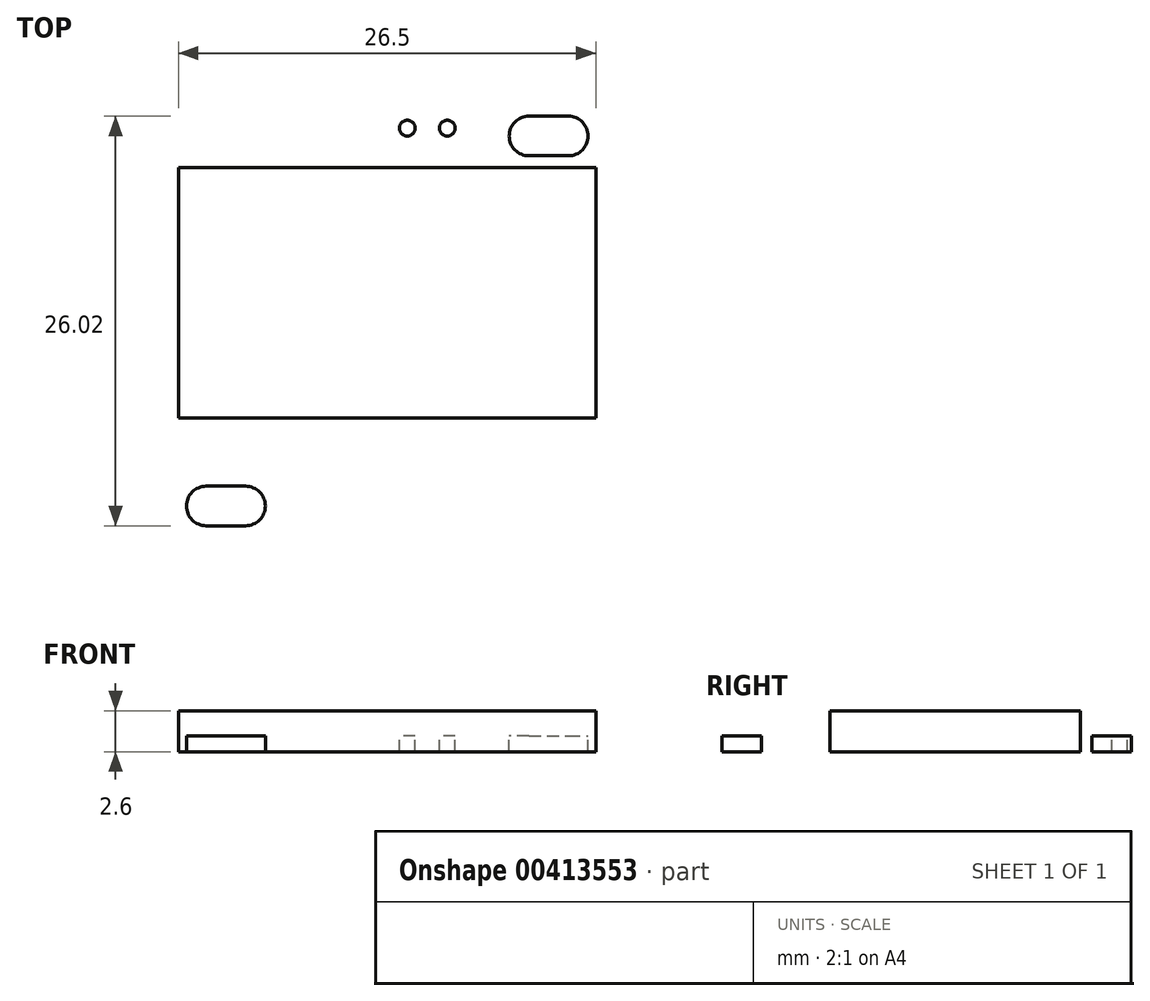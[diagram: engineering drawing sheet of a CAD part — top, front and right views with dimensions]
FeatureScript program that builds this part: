
annotation { "Feature Type Name" : "Feature", "Feature Type Description" : "" }
export const myFeature = defineFeature(function(context is Context, id is Id, definition is map)
    precondition{}
    {
        {
            var Q0;
            Q0=qCreatedBy(makeId("Top.planeOp"),FACE);
            var sketch = newSketch(context, id + "F0", { "sketchPlane" : qUnion([Q0])});
            skLineSegment(sketch, "E0.bottom", {"start": v(13.75, 13.75) * mm, "end": v(-13.75, 13.75) * mm});
            skLineSegment(sketch, "E0.top", {"start": v(13.75, -13.75) * mm, "end": v(-13.75, -13.75) * mm});
            skLineSegment(sketch, "E0.left", {"start": v(13.75, 13.75) * mm, "end": v(13.75, -13.75) * mm});
            skLineSegment(sketch, "E0.right", {"start": v(-13.75, 13.75) * mm, "end": v(-13.75, -13.75) * mm});
            skPoint(sketch, "E0.middle", {"position": v(0, 0) * mm});
            skSolve(sketch);
        }
        {
            var Q0;
            Q0 = qSketchRegion(id + "F0", true);
            extrude(context, id + "F1", {"entities" : qUnion([Q0]), "depth" : 1 * mm});
        }
        {
            var Q0;
            Q0=makeQuery(id+"F1.opExtrude","CAP_FACE",FACE,{"disambiguationData":[OSD([sQuery(id+"F0.wireOp",EDGE,"E0.bottom"),sQuery(id+"F0.wireOp",EDGE,"E0.top"),sQuery(id+"F0.wireOp",EDGE,"E0.left"),sQuery(id+"F0.wireOp",EDGE,"E0.right")])],"isStart":false});
            var sketch = newSketch(context, id + "F2", { "sketchPlane" : qUnion([Q0])});
            skPoint(sketch, "E1.middle", {"position": v(0, 0) * mm});
            skLineSegment(sketch, "E2.bottom", {"start": v(13.25, 9.75) * mm, "end": v(-13.25, 9.75) * mm});
            skLineSegment(sketch, "E2.top", {"start": v(13.25, -6.15) * mm, "end": v(-13.25, -6.15) * mm});
            skLineSegment(sketch, "E2.left", {"start": v(13.25, 9.75) * mm, "end": v(13.25, -6.15) * mm});
            skLineSegment(sketch, "E2.right", {"start": v(-13.25, 9.75) * mm, "end": v(-13.25, -6.15) * mm});
            skPoint(sketch, "E2.middle", {"position": v(0, 1.8) * mm});
            skSolve(sketch);
        }
        {
            var Q0;
            Q0=makeQuery(id+"F2.imprint","IMPRINT",FACE,{"disambiguationData":[TD([[makeQuery(id+"F2.imprint","IMPRINT",EDGE,{"derivedFrom":sQuery(id+"F2.wireOp",EDGE,"E2.bottom")}),1.0]])]});
            extrude(context, id + "F3", {"entities" : qUnion([Q0]), "operationType" : NewBodyOperationType.ADD, "depth" : 1.6 * mm});
        }
        {
            var Q0;
            {var subQ0=sQuery(id+"F0.wireOp",EDGE,"E0.left");var subQ1=sQuery(id+"F0.wireOp",EDGE,"E0.right");var subQ2=sQuery(id+"F0.wireOp",EDGE,"E0.bottom");Q0=makeQuery(id+"F3.boolean.opBoolean","SPLIT",FACE,{"disambiguationData":[TD([makeQuery(id+"F1.opExtrude","SWEPT_FACE",FACE,{"disambiguationData":[OSD([subQ2])]})])],"derivedFrom":makeQuery(id+"F1.opExtrude","CAP_FACE",FACE,{"disambiguationData":[OSD([subQ2,sQuery(id+"F0.wireOp",EDGE,"E0.top"),subQ0,subQ1])],"isStart":false})});}
            var sketch = newSketch(context, id + "F4", { "sketchPlane" : qUnion([Q0])});
            skCircle(sketch, "E3", {"center": v(-1.27, 12.25) * mm, "radius": 0.5 * mm});
            skCircle(sketch, "E4", {"center": v(-3.81, 12.25) * mm, "radius": 0.5 * mm});
            skCircle(sketch, "E5.MirrorC", {"center": v(1.27, 12.25) * mm, "radius": 0.5 * mm});
            skCircle(sketch, "E6.MirrorC", {"center": v(3.81, 12.25) * mm, "radius": 0.5 * mm});
            skLineSegment(sketch, "E7.bottom", {"start": v(-9, 10.5) * mm, "end": v(-11.5, 10.5) * mm});
            skLineSegment(sketch, "E7.top", {"start": v(-9, 13) * mm, "end": v(-11.5, 13) * mm});
            skPoint(sketch, "E7.middle", {"position": v(-10.25, 11.75) * mm});
            skArc(sketch, "E8", {"start": v(-11.5, 10.5) * mm, "mid": v(-12.76, 11.75) * mm, "end": v(-11.5, 13) * mm});
            skArc(sketch, "E9", {"start": v(-9, 10.5) * mm, "mid": v(-7.74, 11.75) * mm, "end": v(-9, 13) * mm});
            skArc(sketch, "E10.MirrorCS", {"start": v(9, 10.5) * mm, "mid": v(7.74, 11.75) * mm, "end": v(9, 13) * mm});
            skLineSegment(sketch, "E11.MirrorCS", {"start": v(9, 10.5) * mm, "end": v(11.5, 10.5) * mm});
            skLineSegment(sketch, "E12.MirrorCS", {"start": v(9, 13) * mm, "end": v(11.5, 13) * mm});
            skArc(sketch, "E13.MirrorCS", {"start": v(11.5, 10.5) * mm, "mid": v(12.76, 11.75) * mm, "end": v(11.5, 13) * mm});
            skArc(sketch, "E14.MirrorCS", {"start": v(-9, -10.5) * mm, "mid": v(-7.74, -11.75) * mm, "end": v(-9, -13) * mm});
            skLineSegment(sketch, "E15.MirrorCS", {"start": v(-9, -10.5) * mm, "end": v(-11.5, -10.5) * mm});
            skLineSegment(sketch, "E16.MirrorCS", {"start": v(-9, -13) * mm, "end": v(-11.5, -13) * mm});
            skArc(sketch, "E17.MirrorCS", {"start": v(-11.5, -10.5) * mm, "mid": v(-12.76, -11.75) * mm, "end": v(-11.5, -13) * mm});
            skLineSegment(sketch, "E18.MirrorCS", {"start": v(9, -13) * mm, "end": v(11.5, -13) * mm});
            skLineSegment(sketch, "E19.MirrorCS", {"start": v(9, -10.5) * mm, "end": v(11.5, -10.5) * mm});
            skArc(sketch, "E20.MirrorCS", {"start": v(9, -10.5) * mm, "mid": v(7.74, -11.75) * mm, "end": v(9, -13) * mm});
            skArc(sketch, "E21.MirrorCS", {"start": v(11.5, -10.5) * mm, "mid": v(12.76, -11.75) * mm, "end": v(11.5, -13) * mm});
            skSolve(sketch);
        }
        {
            var Q0;
            Q0=makeQuery(id+"F4.imprint","IMPRINT",FACE,{"disambiguationData":[TD([[makeQuery(id+"F4.imprint","IMPRINT",EDGE,{"derivedFrom":sQuery(id+"F4.wireOp",EDGE,"E7.bottom")}),-1.0]])]});
            var Q1;
            Q1=makeQuery(id+"F4.imprint","IMPRINT",FACE,{"disambiguationData":[TD([[makeQuery(id+"F4.imprint","IMPRINT",EDGE,{"derivedFrom":sQuery(id+"F4.wireOp",EDGE,"E4")}),1.0]])]});
            var Q2;
            Q2=makeQuery(id+"F4.imprint","IMPRINT",FACE,{"disambiguationData":[TD([[makeQuery(id+"F4.imprint","IMPRINT",EDGE,{"derivedFrom":sQuery(id+"F4.wireOp",EDGE,"E3")}),1.0]])]});
            var Q3;
            Q3=makeQuery(id+"F4.imprint","IMPRINT",FACE,{"disambiguationData":[TD([[makeQuery(id+"F4.imprint","IMPRINT",EDGE,{"derivedFrom":sQuery(id+"F4.wireOp",EDGE,"E5.MirrorC")}),-1.0]])]});
            var Q4;
            Q4=makeQuery(id+"F4.imprint","IMPRINT",FACE,{"disambiguationData":[TD([[makeQuery(id+"F4.imprint","IMPRINT",EDGE,{"derivedFrom":sQuery(id+"F4.wireOp",EDGE,"E6.MirrorC")}),-1.0]])]});
            var Q5;
            Q5=makeQuery(id+"F4.imprint","IMPRINT",FACE,{"disambiguationData":[TD([[makeQuery(id+"F4.imprint","IMPRINT",EDGE,{"derivedFrom":sQuery(id+"F4.wireOp",EDGE,"E10.MirrorCS")}),-1.0]])]});
            var Q6;
            Q6=makeQuery(id+"F4.imprint","IMPRINT",FACE,{"disambiguationData":[TD([[makeQuery(id+"F4.imprint","IMPRINT",EDGE,{"derivedFrom":sQuery(id+"F4.wireOp",EDGE,"E14.MirrorCS")}),-1.0]])]});
            var Q7;
            Q7=makeQuery(id+"F4.imprint","IMPRINT",FACE,{"disambiguationData":[TD([[makeQuery(id+"F4.imprint","IMPRINT",EDGE,{"derivedFrom":sQuery(id+"F4.wireOp",EDGE,"E18.MirrorCS")}),1.0]])]});
            extrude(context, id + "F5", {"entities" : qUnion([Q0, Q1, Q2, Q3, Q4, Q5, Q6, Q7]), "operationType" : NewBodyOperationType.REMOVE, "endBound" : BoundingType.THROUGH_ALL, "oppositeDirection" : true, "depth" : 25 * mm});
        }
        {
            var Q0;
            Q0=makeQuery(id+"F4.imprint","IMPRINT",FACE,{"disambiguationData":[TD([[makeQuery(id+"F4.imprint","IMPRINT",EDGE,{"derivedFrom":sQuery(id+"F4.wireOp",EDGE,"E3")}),-1.0]])]});
            var sketch = newSketch(context, id + "F6", { "sketchPlane" : qUnion([Q0])});
            skText(sketch, "E22", { "text": "VCC", "fontName": "OpenSans-Regular.ttf"});
            skText(sketch, "E23", { "text": "GND", "fontName": "OpenSans-Regular.ttf"});
            skText(sketch, "E24", { "text": "SCL", "fontName": "OpenSans-Regular.ttf"});
            skText(sketch, "E25", { "text": "SDA", "fontName": "OpenSans-Regular.ttf"});
            const initialGuessF6  = {"E22": [-0.00466, 0.01063, 1, 0, 0.00076], "E23": [-0.0022, 0.01073, 1, 0, 0.00065], "E24": [0.00027, 0.01064, 1, 0, 0.00083], "E25": [0.0029, 0.01068, 1, 0, 0.00073]};
            skSetInitialGuess(sketch, initialGuessF6);
            skSolve(sketch);
        }
        {
            var Q0;
            Q0 = qSketchRegion(id + "F6", true);
            extrude(context, id + "F7", {"entities" : qUnion([Q0]), "operationType" : NewBodyOperationType.REMOVE, "oppositeDirection" : true, "depth" : 0.1 * mm});
        }
    });
